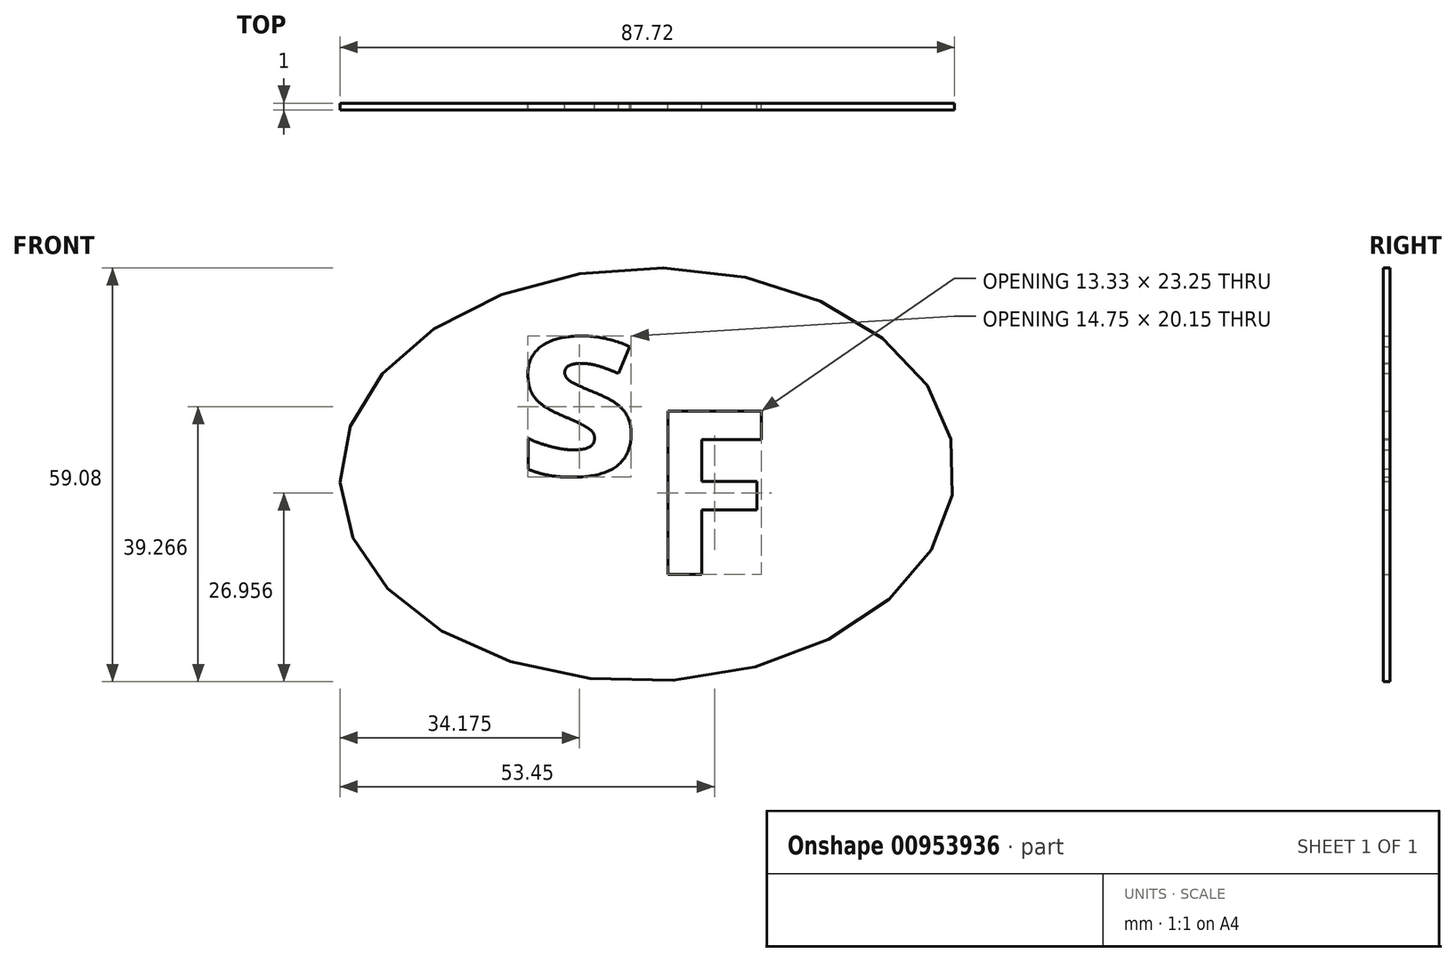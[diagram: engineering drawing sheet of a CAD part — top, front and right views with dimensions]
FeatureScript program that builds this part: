
annotation { "Feature Type Name" : "Feature", "Feature Type Description" : "" }
export const myFeature = defineFeature(function(context is Context, id is Id, definition is map)
    precondition{}
    {
        {
            var Q0;
            Q0=qCreatedBy(makeId("Front.planeOp"),FACE);
            var sketch = newSketch(context, id + "F0", { "sketchPlane" : qUnion([Q0])});
            skEllipse(sketch, "E0", {"center": v(0, 0) * mm, "majorRadius": 43.87 * mm, "minorRadius": 29.53 * mm, "majorAxis": v(-1, -0.02)});
            skText(sketch, "E1", { "text": "s", "fontName": "OpenSans-Bold.ttf"});
            skText(sketch, "E2", { "text": "F", "fontName": "OpenSans-Bold.ttf"});
            const initialGuessF0  = {"E1": [-0.01866, 0, 1, 0, 0.02564], "E2": [0, -0.01421, 1, 0, 0.02345]};
            skSetInitialGuess(sketch, initialGuessF0);
            skSolve(sketch);
        }
        {
            var Q0;
            Q0=makeQuery(id+"F0.imprint","IMPRINT",FACE,{"disambiguationData":[TD([[makeQuery(id+"F0.imprint","IMPRINT",EDGE,{"derivedFrom":sQuery(id+"F0.wireOp",EDGE,"E0")}),1.0]])]});
            extrude(context, id + "F1", {"entities" : qUnion([Q0]), "depth" : 1 * mm, "offsetDistance" : 25.4 * mm});
        }
    });
